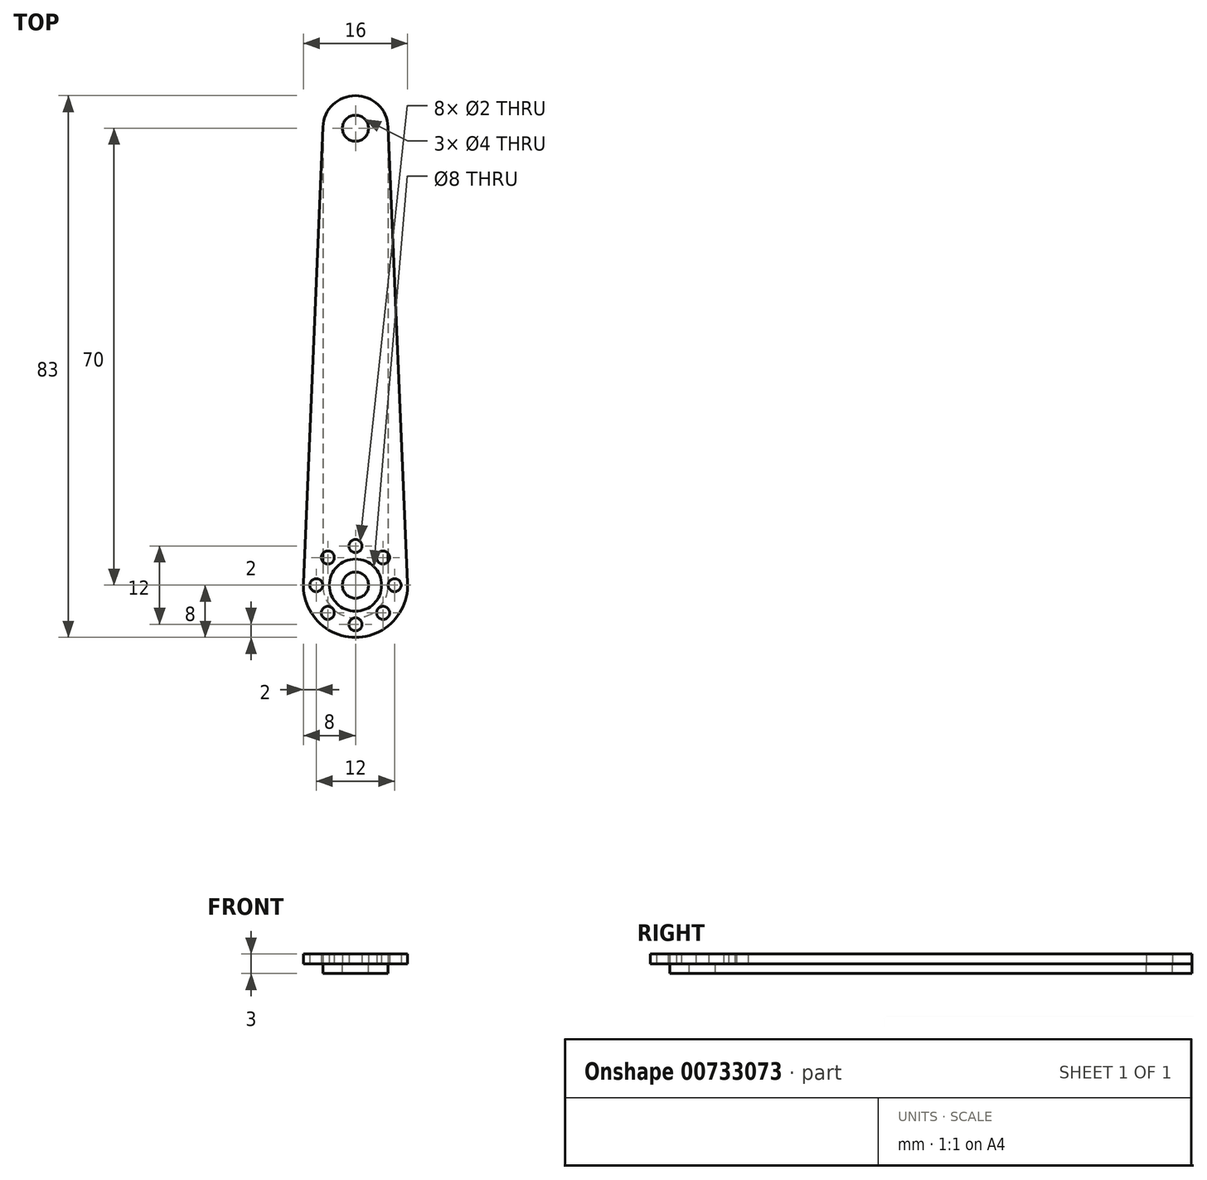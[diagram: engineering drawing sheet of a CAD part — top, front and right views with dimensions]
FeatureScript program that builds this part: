
annotation { "Feature Type Name" : "Feature", "Feature Type Description" : "" }
export const myFeature = defineFeature(function(context is Context, id is Id, definition is map)
    precondition{}
    {
        {
            var Q0;
            Q0=qCreatedBy(makeId("Top.planeOp"),FACE);
            var sketch = newSketch(context, id + "F0", { "sketchPlane" : qUnion([Q0])});
            skArc(sketch, "E0", {"start": v(-8, 0.34) * mm, "mid": v(0, -8) * mm, "end": v(8, 0.34) * mm});
            skCircle(sketch, "E1", {"center": v(0, 0) * mm, "radius": 4 * mm});
            skCircle(sketch, "E2", {"center": v(6, 0) * mm, "radius": 1 * mm});
            skCircle(sketch, "E3.1.0", {"center": v(4.24, 4.24) * mm, "radius": 1 * mm});
            skCircle(sketch, "E3.2.0", {"center": v(0, 6) * mm, "radius": 1 * mm});
            skCircle(sketch, "E3.3.0", {"center": v(-4.24, 4.24) * mm, "radius": 1 * mm});
            skCircle(sketch, "E3.4.0", {"center": v(-6, 0) * mm, "radius": 1 * mm});
            skCircle(sketch, "E3.5.0", {"center": v(-4.24, -4.24) * mm, "radius": 1 * mm});
            skCircle(sketch, "E3.6.0", {"center": v(0, -6) * mm, "radius": 1 * mm});
            skCircle(sketch, "E3.7.0", {"center": v(4.24, -4.24) * mm, "radius": 1 * mm});
            skCircle(sketch, "E4", {"center": v(0, 70) * mm, "radius": 2 * mm});
            skArc(sketch, "E5", {"start": v(5, 70.21) * mm, "mid": v(0, 75) * mm, "end": v(-5, 70.21) * mm});
            skLineSegment(sketch, "E6", {"start": v(-5, 70.21) * mm, "end": v(-8, 0.34) * mm});
            skLineSegment(sketch, "E7.MirrorCS", {"start": v(5, 70.21) * mm, "end": v(8, 0.34) * mm});
            skSolve(sketch);
        }
        {
            var Q0;
            Q0=qSketchRegion(id+"F0",true);
            extrude(context, id + "F1", {"entities" : qUnion([Q0]), "depth" : 1.5 * mm, "offsetDistance" : 25 * mm});
        }
        {
            var Q0;
            Q0=qCreatedBy(makeId("Top.planeOp"),FACE);
            var sketch = newSketch(context, id + "F2", { "sketchPlane" : qUnion([Q0])});
            skCircle(sketch, "E8.0", {"center": v(0, 70) * mm, "radius": 2 * mm});
            skArc(sketch, "E9", {"start": v(5, 70) * mm, "mid": v(0, 75) * mm, "end": v(-5, 70) * mm});
            skLineSegment(sketch, "E10", {"start": v(0, 70) * mm, "end": v(0, 0) * mm, "construction": true});
            skLineSegment(sketch, "E11", {"start": v(0, 35) * mm, "end": v(-5, 35) * mm, "construction": true});
            skPoint(sketch, "E12", {"position": v(-5, 70) * mm});
            skPoint(sketch, "E13.MirrorP", {"position": v(5, 70) * mm});
            skLineSegment(sketch, "E14", {"start": v(-5, 70) * mm, "end": v(-5, 35) * mm});
            skLineSegment(sketch, "E15.MirrorCS", {"start": v(5, 70) * mm, "end": v(5, 35) * mm});
            skLineSegment(sketch, "E16.MirrorCS", {"start": v(-5, 0) * mm, "end": v(-5, 35) * mm});
            skCircle(sketch, "E17.MirrorC", {"center": v(0, 0) * mm, "radius": 2 * mm});
            skArc(sketch, "E18.MirrorCS", {"start": v(5, 0) * mm, "mid": v(0, -5) * mm, "end": v(-5, 0) * mm});
            skLineSegment(sketch, "E19.MirrorCS", {"start": v(5, 0) * mm, "end": v(5, 35) * mm});
            skSolve(sketch);
        }
        {
            var Q0;
            Q0=qSketchRegion(id+"F2",true);
            extrude(context, id + "F3", {"entities" : qUnion([Q0]), "oppositeDirection" : true, "depth" : 1.5 * mm, "offsetDistance" : 25 * mm});
        }
    });
